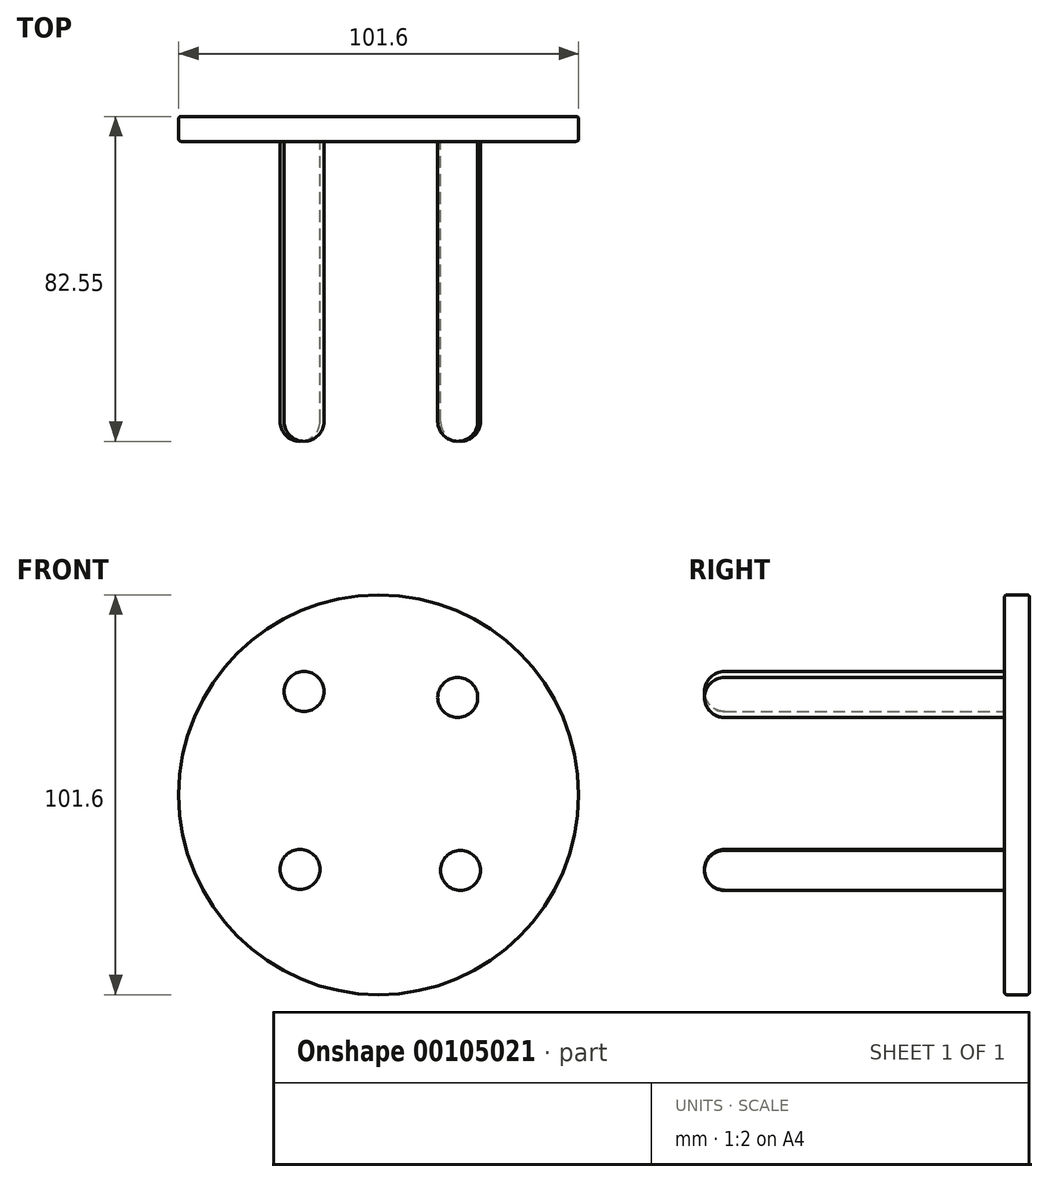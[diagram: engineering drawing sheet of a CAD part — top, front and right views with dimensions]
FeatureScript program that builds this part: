
annotation { "Feature Type Name" : "Feature", "Feature Type Description" : "" }
export const myFeature = defineFeature(function(context is Context, id is Id, definition is map)
    precondition{}
    {
        {
            var Q0;
            Q0=qCreatedBy(makeId("Front.planeOp"),FACE);
            var sketch = newSketch(context, id + "F0", { "sketchPlane" : qUnion([Q0])});
            skCircle(sketch, "E0", {"center": v(0, 0) * mm, "radius": 50.8 * mm});
            skLineSegment(sketch, "E1", {"start": v(0, 0) * mm, "end": v(50.8, 0) * mm});
            skLineSegment(sketch, "E2", {"start": v(0, 0) * mm, "end": v(0, 50.8) * mm});
            skCircle(sketch, "E3", {"center": v(19.05, 25.4) * mm, "radius": 6.35 * mm});
            skSolve(sketch);
        }
        {
            var Q0;
            Q0=makeQuery(id+"F0.imprint","IMPRINT",FACE,{"disambiguationData":[TD([[makeQuery(id+"F0.imprint","IMPRINT",EDGE,{"derivedFrom":sQuery(id+"F0.wireOp",EDGE,"E0")}),1.0]])]});
            var Q1;
            {var subQ0=sQuery(id+"F0.wireOp",EDGE,"E1");Q1=makeQuery(id+"F0.imprint","IMPRINT",FACE,{"disambiguationData":[TD([[makeQuery(id+"F0.imprint","IMPRINT",EDGE,{"derivedFrom":subQ0}),1.0]])]});}
            var Q2;
            Q2=makeQuery(id+"F0.imprint","IMPRINT",FACE,{"disambiguationData":[TD([[makeQuery(id+"F0.imprint","IMPRINT",EDGE,{"derivedFrom":sQuery(id+"F0.wireOp",EDGE,"E3")}),1.0]])]});
            extrude(context, id + "F1", {"entities" : qUnion([Q0, Q1, Q2]), "depth" : 6.35 * mm});
        }
        {
            var Q0;
            Q0=makeQuery(id+"F1.opExtrude","CAP_EDGE",EDGE,{"disambiguationData":[OSD([sQuery(id+"F0.wireOp",EDGE,"E0")])],"isStart":false});
            var Q1;
            Q1=makeQuery(id+"F1.opExtrude","CAP_EDGE",EDGE,{"disambiguationData":[OSD([sQuery(id+"F0.wireOp",EDGE,"E0")])],"isStart":true});
            fillet(context, id + "F2", {"entities" : qUnion([Q0, Q1]), "radius" : 0.64 * mm, "tangentPropagation" : true, "allowEdgeOverflow" : false});
        }
        {
            var Q0;
            Q0=makeQuery(id+"F1.opExtrude","CAP_FACE",FACE,{"disambiguationData":[OSD([sQuery(id+"F0.wireOp",EDGE,"E0")])],"isStart":false});
            var sketch = newSketch(context, id + "F3", { "sketchPlane" : qUnion([Q0])});
            skCircle(sketch, "E4", {"center": v(20.09, 24.7) * mm, "radius": 5.08 * mm});
            skCircle(sketch, "E5", {"center": v(20.77, -19.21) * mm, "radius": 5.08 * mm});
            skCircle(sketch, "E6", {"center": v(-20, -18.95) * mm, "radius": 5.08 * mm});
            skCircle(sketch, "E7", {"center": v(-18.95, 26.22) * mm, "radius": 5.08 * mm});
            skSolve(sketch);
        }
        {
            var Q0;
            Q0=makeQuery(id+"F3.imprint","IMPRINT",FACE,{"disambiguationData":[TD([[makeQuery(id+"F3.imprint","IMPRINT",EDGE,{"derivedFrom":sQuery(id+"F3.wireOp",EDGE,"E4")}),1.0]])]});
            extrude(context, id + "F4", {"entities" : qUnion([Q0]), "operationType" : NewBodyOperationType.ADD, "depth" : 76.2 * mm});
        }
        {
            var Q0;
            Q0 = qSketchRegion(id + "F3", true);
            extrude(context, id + "F5", {"entities" : qUnion([Q0]), "operationType" : NewBodyOperationType.ADD, "depth" : 76.2 * mm});
        }
        {
            var Q0;
            Q0=makeQuery(id+"F5.opExtrude","CAP_EDGE",EDGE,{"disambiguationData":[OSD([sQuery(id+"F3.wireOp",EDGE,"E7")])],"isStart":false});
            var Q1;
            Q1=makeQuery(id+"F4.opExtrude","CAP_EDGE",EDGE,{"disambiguationData":[OSD([sQuery(id+"F3.wireOp",EDGE,"E4")])],"isStart":false});
            var Q2;
            Q2=makeQuery(id+"F5.opExtrude","CAP_EDGE",EDGE,{"disambiguationData":[OSD([sQuery(id+"F3.wireOp",EDGE,"E6")])],"isStart":false});
            var Q3;
            Q3=makeQuery(id+"F5.opExtrude","CAP_EDGE",EDGE,{"disambiguationData":[OSD([sQuery(id+"F3.wireOp",EDGE,"E5")])],"isStart":false});
            fillet(context, id + "F6", {"entities" : qUnion([Q0, Q1, Q2, Q3]), "radius" : 5.08 * mm, "tangentPropagation" : true, "allowEdgeOverflow" : false});
        }
    });
